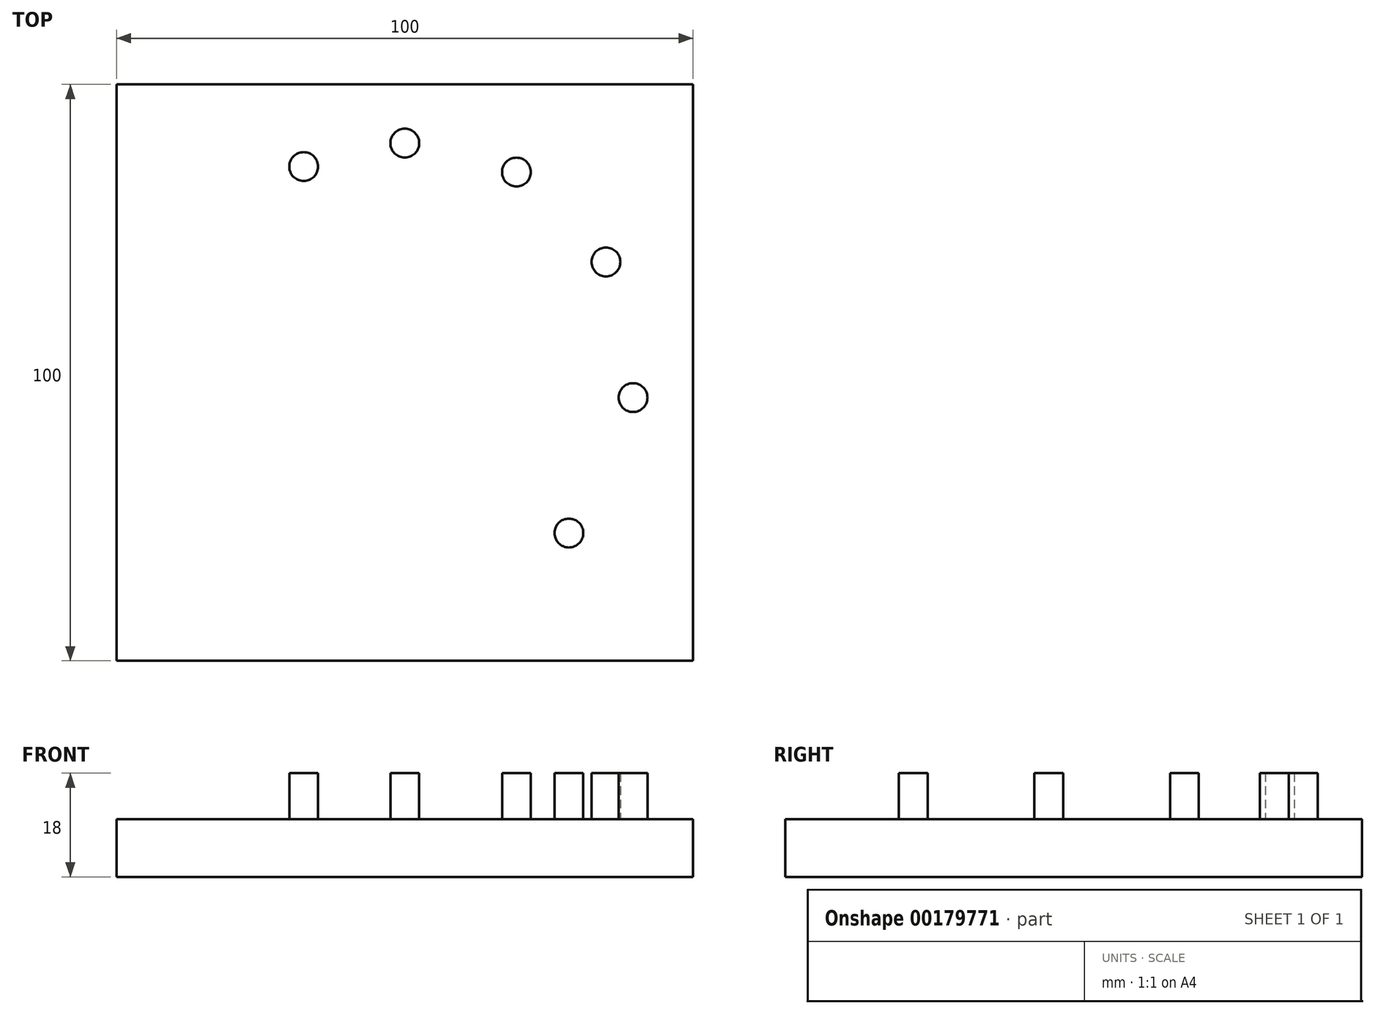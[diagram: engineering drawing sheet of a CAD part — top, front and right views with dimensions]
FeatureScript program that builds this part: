
annotation { "Feature Type Name" : "Feature", "Feature Type Description" : "" }
export const myFeature = defineFeature(function(context is Context, id is Id, definition is map)
    precondition{}
    {
        {
            var Q0;
            Q0=qCreatedBy(makeId("Top.planeOp"),FACE);
            var sketch = newSketch(context, id + "F0", { "sketchPlane" : qUnion([Q0])});
            skLineSegment(sketch, "E0.bottom", {"start": v(-50, 50) * mm, "end": v(50, 50) * mm});
            skLineSegment(sketch, "E0.top", {"start": v(-50, -50) * mm, "end": v(50, -50) * mm});
            skLineSegment(sketch, "E0.left", {"start": v(-50, 50) * mm, "end": v(-50, -50) * mm});
            skLineSegment(sketch, "E0.right", {"start": v(50, 50) * mm, "end": v(50, -50) * mm});
            skSolve(sketch);
        }
        {
            var Q0;
            Q0 = qSketchRegion(id + "F0", true);
            extrude(context, id + "F1", {"entities" : qUnion([Q0]), "depth" : 10 * mm});
        }
        {
            var Q0;
            Q0=makeQuery(id+"F1.opExtrude","CAP_FACE",FACE,{"disambiguationData":[OSD([sQuery(id+"F0.wireOp",EDGE,"E0.bottom"),sQuery(id+"F0.wireOp",EDGE,"E0.top"),sQuery(id+"F0.wireOp",EDGE,"E0.left"),sQuery(id+"F0.wireOp",EDGE,"E0.right")])],"isStart":false});
            var sketch = newSketch(context, id + "F2", { "sketchPlane" : qUnion([Q0])});
            skCircle(sketch, "E1", {"center": v(-17.53, 35.74) * mm, "radius": 2.5 * mm});
            skCircle(sketch, "E2", {"center": v(0, 39.81) * mm, "radius": 2.5 * mm});
            skCircle(sketch, "E3", {"center": v(19.36, 34.79) * mm, "radius": 2.5 * mm});
            skCircle(sketch, "E4", {"center": v(34.88, 19.2) * mm, "radius": 2.5 * mm});
            skCircle(sketch, "E5", {"center": v(39.58, -4.34) * mm, "radius": 2.5 * mm});
            skCircle(sketch, "E6", {"center": v(28.46, -27.84) * mm, "radius": 2.5 * mm});
            skLineSegment(sketch, "E7", {"start": v(-17.53, 35.74) * mm, "end": v(0, 39.81) * mm});
            skLineSegment(sketch, "E8", {"start": v(0, 39.81) * mm, "end": v(19.36, 34.79) * mm});
            skLineSegment(sketch, "E9", {"start": v(19.36, 34.79) * mm, "end": v(34.88, 19.2) * mm});
            skLineSegment(sketch, "E10", {"start": v(34.88, 19.2) * mm, "end": v(39.58, -4.34) * mm});
            skLineSegment(sketch, "E11", {"start": v(39.58, -4.34) * mm, "end": v(28.46, -27.84) * mm});
            skSolve(sketch);
        }
        {
            var Q0;
            Q0 = qSketchRegion(id + "F2", true);
            extrude(context, id + "F3", {"entities" : qUnion([Q0]), "operationType" : NewBodyOperationType.ADD, "depth" : 8 * mm});
        }
    });
